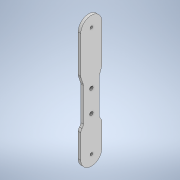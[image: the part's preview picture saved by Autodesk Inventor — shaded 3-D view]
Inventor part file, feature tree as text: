
AUTODESK INVENTOR PART (.ipt)
format: ipt  version: 2022 (Build 260153000, 153)  size: 156,672 bytes
history: native  units: mm
features: extrude x1, sketch x1
ambient origin geometry x8: Origin, YZ Plane, XZ Plane, XY Plane, X Axis, Y Axis, Z Axis, Center Point
bodies: Solid1 (feature_tree)
feature tree (2):
  extrude  "Extrusion1"  Depth=5.0mm
  sketch  "Sketch1"  dims[d16=3.0mm d17=0.0mm d44=4.0mm d46=8.0mm d47=9.0mm d48=9.0mm d50=8.0mm d53=24.0mm d54=3.0mm d57=4.0mm d59=8.0mm d60=9.0mm d61=9.0mm d63=8.0mm d64=40.0mm d65=25.0mm d100=5.0mm d102=3.0mm d103=60.0mm d104=0.872665mm d105=0.5mm d106=0.872665mm]
